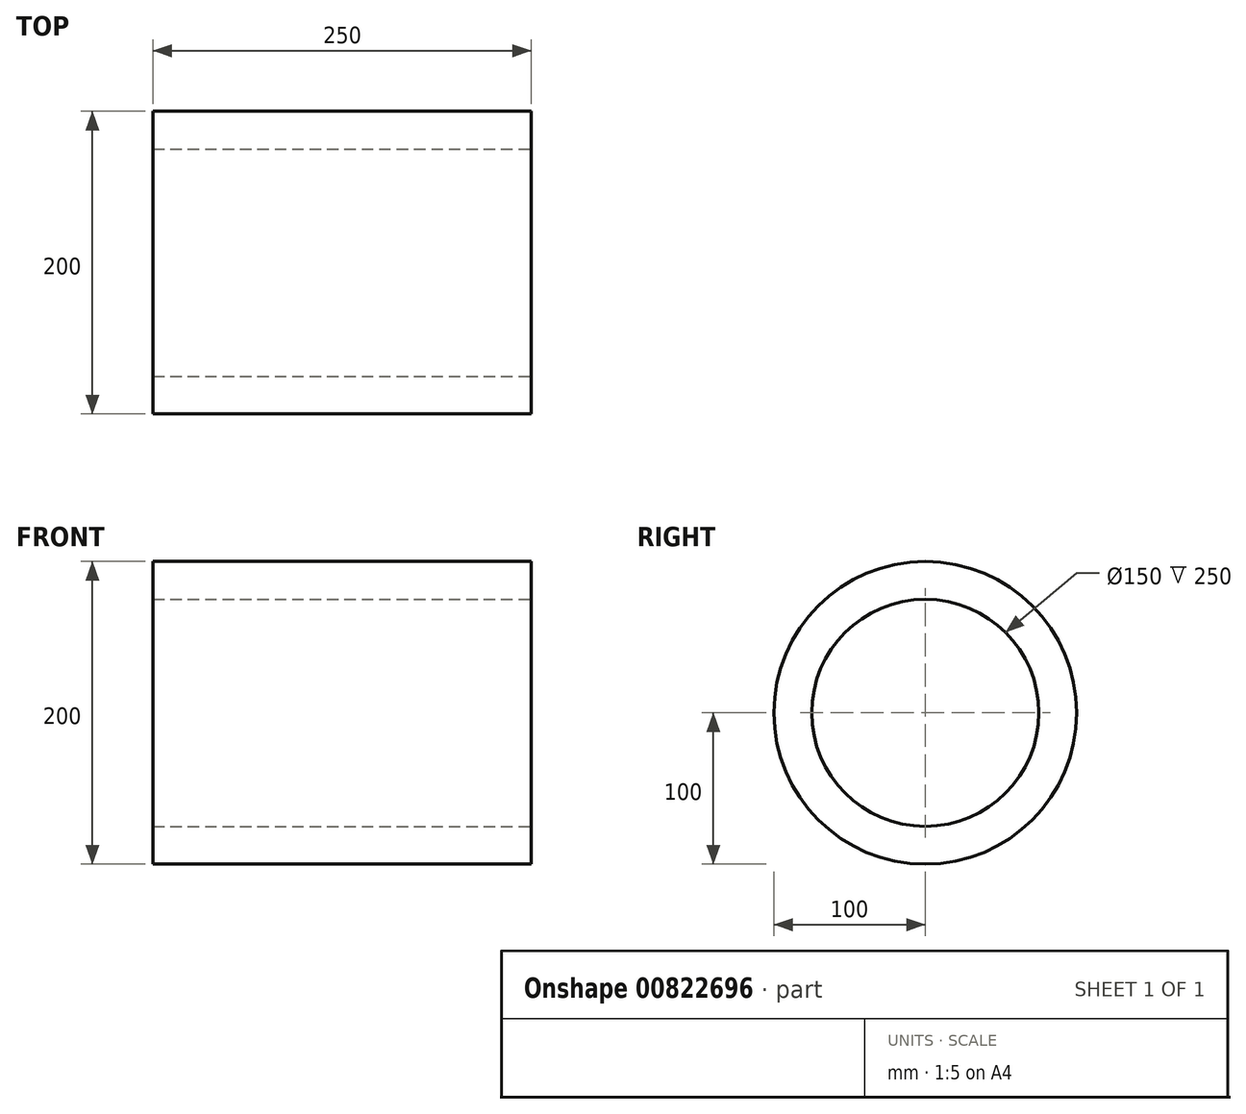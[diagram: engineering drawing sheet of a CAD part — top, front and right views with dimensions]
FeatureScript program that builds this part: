
annotation { "Feature Type Name" : "Feature", "Feature Type Description" : "" }
export const myFeature = defineFeature(function(context is Context, id is Id, definition is map)
    precondition{}
    {
        {
            var Q0;
            Q0=qCreatedBy(makeId("Right.planeOp"),FACE);
            var sketch = newSketch(context, id + "F0", { "sketchPlane" : qUnion([Q0])});
            skCircle(sketch, "E0", {"center": v(0, 0) * mm, "radius": 750 * mm});
            skCircle(sketch, "E1", {"center": v(0, 0) * mm, "radius": 75 * mm});
            skCircle(sketch, "E2", {"center": v(0, 0) * mm, "radius": 100 * mm});
            skSolve(sketch);
        }
        {
            var Q0;
            Q0=makeQuery(id+"F0.imprint","IMPRINT",FACE,{"disambiguationData":[TD([[makeQuery(id+"F0.imprint","IMPRINT",EDGE,{"derivedFrom":sQuery(id+"F0.wireOp",EDGE,"E1")}),-1.0]])]});
            extrude(context, id + "F1", {"entities" : qUnion([Q0]), "oppositeDirection" : true, "depth" : 250 * mm, "offsetDistance" : 25 * mm});
        }
    });
